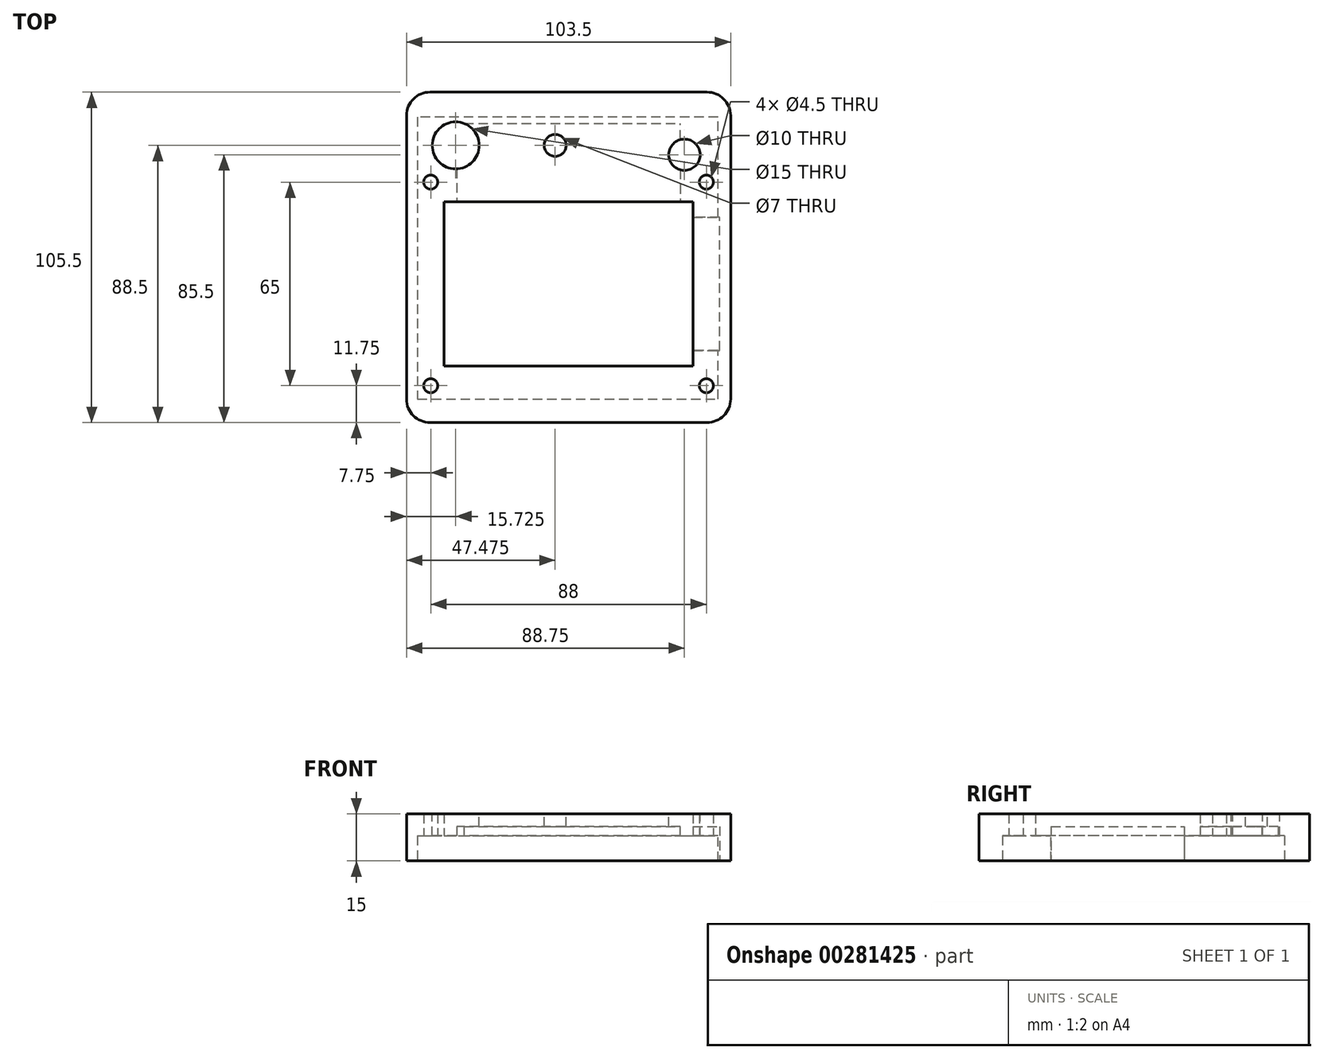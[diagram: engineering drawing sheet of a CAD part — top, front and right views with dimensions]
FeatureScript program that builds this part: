
annotation { "Feature Type Name" : "Feature", "Feature Type Description" : "" }
export const myFeature = defineFeature(function(context is Context, id is Id, definition is map)
    precondition{}
    {
        {
            var Q0;
            Q0=qCreatedBy(makeId("Top.planeOp"),FACE);
            var sketch = newSketch(context, id + "F0", { "sketchPlane" : qUnion([Q0])});
            skLineSegment(sketch, "E0.rect.bottom", {"start": v(44, -32.5) * mm, "end": v(-44, -32.5) * mm, "construction": true});
            skLineSegment(sketch, "E0.rect.top", {"start": v(44, 32.5) * mm, "end": v(-44, 32.5) * mm, "construction": true});
            skLineSegment(sketch, "E0.rect.left", {"start": v(44, -32.5) * mm, "end": v(44, 32.5) * mm, "construction": true});
            skLineSegment(sketch, "E0.rect.right", {"start": v(-44, -32.5) * mm, "end": v(-44, 32.5) * mm, "construction": true});
            skPoint(sketch, "E0.rect.middle", {"position": v(0, 0) * mm});
            skCircle(sketch, "E1", {"center": v(-44, 32.5) * mm, "radius": 2.25 * mm});
            skCircle(sketch, "E2", {"center": v(44, 32.5) * mm, "radius": 2.25 * mm});
            skCircle(sketch, "E3", {"center": v(-44, -32.5) * mm, "radius": 2.25 * mm});
            skCircle(sketch, "E4", {"center": v(44, -32.5) * mm, "radius": 2.25 * mm});
            skLineSegment(sketch, "E5.rect.bottom", {"start": v(39.75, -26.25) * mm, "end": v(-39.75, -26.25) * mm});
            skLineSegment(sketch, "E5.rect.top", {"start": v(39.75, 26.25) * mm, "end": v(-39.75, 26.25) * mm});
            skLineSegment(sketch, "E5.rect.left", {"start": v(39.75, -26.25) * mm, "end": v(39.75, 26.25) * mm});
            skLineSegment(sketch, "E5.rect.right", {"start": v(-39.75, -26.25) * mm, "end": v(-39.75, 26.25) * mm});
            skLineSegment(sketch, "E6", {"start": v(-51.75, -44.25) * mm, "end": v(51.75, -44.25) * mm});
            skLineSegment(sketch, "E7", {"start": v(51.75, -44.25) * mm, "end": v(51.75, 61.25) * mm});
            skLineSegment(sketch, "E8", {"start": v(-3.25, 61.25) * mm, "end": v(-51.75, 61.25) * mm});
            skLineSegment(sketch, "E9", {"start": v(-51.75, 61.25) * mm, "end": v(-51.75, -9.25) * mm});
            skLineSegment(sketch, "E10", {"start": v(-51.75, -9.25) * mm, "end": v(-71.75, -9.25) * mm, "construction": true});
            skLineSegment(sketch, "E11", {"start": v(-71.75, -9.25) * mm, "end": v(-71.75, -44.25) * mm, "construction": true});
            skLineSegment(sketch, "E12", {"start": v(-71.75, -44.25) * mm, "end": v(-51.75, -44.25) * mm, "construction": true});
            skLineSegment(sketch, "E13", {"start": v(11.75, 61.25) * mm, "end": v(11.75, 91.25) * mm, "construction": true});
            skLineSegment(sketch, "E14", {"start": v(11.75, 91.25) * mm, "end": v(51.75, 91.25) * mm, "construction": true});
            skLineSegment(sketch, "E15", {"start": v(51.75, 91.25) * mm, "end": v(51.75, 61.25) * mm, "construction": true});
            skCircle(sketch, "E16", {"center": v(44.25, 83.75) * mm, "radius": 2.12 * mm, "construction": true});
            skCircle(sketch, "E17", {"center": v(-64.25, -16.75) * mm, "radius": 2.12 * mm, "construction": true});
            skCircle(sketch, "E18", {"center": v(-64.25, -36.75) * mm, "radius": 2.12 * mm, "construction": true});
            skCircle(sketch, "E19", {"center": v(4.25, 83.75) * mm, "radius": 2.12 * mm, "construction": true});
            skLineSegment(sketch, "E20", {"start": v(11.75, 61.25) * mm, "end": v(51.75, 61.25) * mm});
            skLineSegment(sketch, "E21", {"start": v(11.75, 91.25) * mm, "end": v(-3.25, 91.25) * mm, "construction": true});
            skLineSegment(sketch, "E22", {"start": v(-3.25, 91.25) * mm, "end": v(-3.25, 61.25) * mm, "construction": true});
            skLineSegment(sketch, "E23", {"start": v(-3.25, 61.25) * mm, "end": v(11.75, 61.25) * mm});
            skLineSegment(sketch, "E24", {"start": v(-51.75, -9.25) * mm, "end": v(-51.75, -44.25) * mm});
            skSolve(sketch);
        }
        {
            var Q0;
            Q0=qSketchRegion(id+"F0",true);
            extrude(context, id + "F1", {"entities" : qUnion([Q0]), "depth" : 15 * mm});
        }
        {
            var Q0;
            Q0=makeQuery(id+"F1.opExtrude","CAP_FACE",FACE,{"disambiguationData":[OSD([sQuery(id+"F0.wireOp",EDGE,"E1"),sQuery(id+"F0.wireOp",EDGE,"E2"),sQuery(id+"F0.wireOp",EDGE,"E3"),sQuery(id+"F0.wireOp",EDGE,"E4"),sQuery(id+"F0.wireOp",EDGE,"35a865c8-fce7-4a90-a9e5-dcc01825e7bf.rect.bottom"),sQuery(id+"F0.wireOp",EDGE,"35a865c8-fce7-4a90-a9e5-dcc01825e7bf.rect.top"),sQuery(id+"F0.wireOp",EDGE,"35a865c8-fce7-4a90-a9e5-dcc01825e7bf.rect.left"),sQuery(id+"F0.wireOp",EDGE,"35a865c8-fce7-4a90-a9e5-dcc01825e7bf.rect.right"),sQuery(id+"F0.wireOp",EDGE,"E5.rect.bottom"),sQuery(id+"F0.wireOp",EDGE,"E5.rect.top"),sQuery(id+"F0.wireOp",EDGE,"E5.rect.left"),sQuery(id+"F0.wireOp",EDGE,"E5.rect.right")])],"isStart":true});
            var sketch = newSketch(context, id + "F2", { "sketchPlane" : qUnion([Q0])});
            skLineSegment(sketch, "E25", {"start": v(39.75, 21.25) * mm, "end": v(48.25, 21.25) * mm});
            skLineSegment(sketch, "E26", {"start": v(48.25, 21.25) * mm, "end": v(48.25, -21.25) * mm});
            skLineSegment(sketch, "E27", {"start": v(48.25, -21.25) * mm, "end": v(39.75, -21.25) * mm});
            skLineSegment(sketch, "E28", {"start": v(39.75, -21.25) * mm, "end": v(39.75, 21.25) * mm});
            skLineSegment(sketch, "E29", {"start": v(-35.75, -26.25) * mm, "end": v(-35.75, -51.25) * mm});
            skLineSegment(sketch, "E30", {"start": v(-35.75, -51.25) * mm, "end": v(35.75, -51.25) * mm});
            skLineSegment(sketch, "E31", {"start": v(35.75, -51.25) * mm, "end": v(35.75, -26.25) * mm});
            skLineSegment(sketch, "E32", {"start": v(35.75, -26.25) * mm, "end": v(-35.75, -26.25) * mm});
            skSolve(sketch);
        }
        {
            var Q0;
            Q0=qSketchRegion(id+"F2",true);
            extrude(context, id + "F3", {"entities" : qUnion([Q0]), "operationType" : NewBodyOperationType.REMOVE, "oppositeDirection" : true, "depth" : 11 * mm});
        }
        {
            var Q0;
            Q0=makeQuery(id+"F1.opExtrude","CAP_FACE",FACE,{"disambiguationData":[OSD([sQuery(id+"F0.wireOp",EDGE,"E1"),sQuery(id+"F0.wireOp",EDGE,"E2"),sQuery(id+"F0.wireOp",EDGE,"E3"),sQuery(id+"F0.wireOp",EDGE,"E4"),sQuery(id+"F0.wireOp",EDGE,"35a865c8-fce7-4a90-a9e5-dcc01825e7bf.rect.bottom"),sQuery(id+"F0.wireOp",EDGE,"35a865c8-fce7-4a90-a9e5-dcc01825e7bf.rect.top"),sQuery(id+"F0.wireOp",EDGE,"35a865c8-fce7-4a90-a9e5-dcc01825e7bf.rect.left"),sQuery(id+"F0.wireOp",EDGE,"35a865c8-fce7-4a90-a9e5-dcc01825e7bf.rect.right"),sQuery(id+"F0.wireOp",EDGE,"E5.rect.bottom"),sQuery(id+"F0.wireOp",EDGE,"E5.rect.top"),sQuery(id+"F0.wireOp",EDGE,"E5.rect.left"),sQuery(id+"F0.wireOp",EDGE,"E5.rect.right")])],"isStart":true});
            var sketch = newSketch(context, id + "F4", { "sketchPlane" : qUnion([Q0])});
            skLineSegment(sketch, "E33", {"start": v(-48.25, 36.75) * mm, "end": v(47.75, 36.75) * mm});
            skLineSegment(sketch, "E34", {"start": v(47.75, 36.75) * mm, "end": v(47.75, -53.25) * mm});
            skLineSegment(sketch, "E35", {"start": v(47.75, -53.25) * mm, "end": v(-48.25, -53.25) * mm});
            skLineSegment(sketch, "E36", {"start": v(-48.25, -53.25) * mm, "end": v(-48.25, 36.75) * mm});
            skSolve(sketch);
        }
        {
            var Q0;
            Q0=qSketchRegion(id+"F4",true);
            extrude(context, id + "F5", {"entities" : qUnion([Q0]), "operationType" : NewBodyOperationType.REMOVE, "oppositeDirection" : true, "depth" : 8 * mm});
        }
        {
            var Q0;
            Q0=makeQuery(id+"F1.opExtrude","CAP_FACE",FACE,{"disambiguationData":[OSD([sQuery(id+"F0.wireOp",EDGE,"E1"),sQuery(id+"F0.wireOp",EDGE,"E2"),sQuery(id+"F0.wireOp",EDGE,"E3"),sQuery(id+"F0.wireOp",EDGE,"E4"),sQuery(id+"F0.wireOp",EDGE,"35a865c8-fce7-4a90-a9e5-dcc01825e7bf.rect.bottom"),sQuery(id+"F0.wireOp",EDGE,"35a865c8-fce7-4a90-a9e5-dcc01825e7bf.rect.top"),sQuery(id+"F0.wireOp",EDGE,"35a865c8-fce7-4a90-a9e5-dcc01825e7bf.rect.left"),sQuery(id+"F0.wireOp",EDGE,"35a865c8-fce7-4a90-a9e5-dcc01825e7bf.rect.right"),sQuery(id+"F0.wireOp",EDGE,"E5.rect.bottom"),sQuery(id+"F0.wireOp",EDGE,"E5.rect.top"),sQuery(id+"F0.wireOp",EDGE,"E5.rect.left"),sQuery(id+"F0.wireOp",EDGE,"E5.rect.right")])],"isStart":false});
            var sketch = newSketch(context, id + "F6", { "sketchPlane" : qUnion([Q0])});
            skCircle(sketch, "E37", {"center": v(-36.02, 44.25) * mm, "radius": 7.5 * mm});
            skCircle(sketch, "E38", {"center": v(-4.27, 44.25) * mm, "radius": 3.5 * mm});
            skCircle(sketch, "E39", {"center": v(37, 41.25) * mm, "radius": 5 * mm});
            skSolve(sketch);
        }
        {
            var Q0;
            Q0=qSketchRegion(id+"F6",true);
            extrude(context, id + "F7", {"entities" : qUnion([Q0]), "operationType" : NewBodyOperationType.REMOVE, "endBound" : BoundingType.THROUGH_ALL, "oppositeDirection" : true, "depth" : 25 * mm});
        }
        {
            var Q0;
            Q0=makeQuery(id+"F1.opExtrude","SWEPT_EDGE",EDGE,{"disambiguationData":[OSD([sQuery(id+"F0.wireOp",EDGE,"E6"),sQuery(id+"F0.wireOp",EDGE,"E7")])]});
            var Q1;
            Q1=makeQuery(id+"F1.opExtrude","SWEPT_EDGE",EDGE,{"disambiguationData":[OSD([sQuery(id+"F0.wireOp",EDGE,"E6"),sQuery(id+"F0.wireOp",EDGE,"E9")])]});
            var Q2;
            Q2=makeQuery(id+"F1.opExtrude","SWEPT_EDGE",EDGE,{"disambiguationData":[OSD([sQuery(id+"F0.wireOp",EDGE,"E7"),sQuery(id+"F0.wireOp",EDGE,"E8")])]});
            var Q3;
            Q3=makeQuery(id+"F1.opExtrude","SWEPT_EDGE",EDGE,{"disambiguationData":[OSD([sQuery(id+"F0.wireOp",EDGE,"E8"),sQuery(id+"F0.wireOp",EDGE,"E9")])]});
            var Q4;
            Q4=makeQuery(id+"F1.opExtrude","SWEPT_EDGE",EDGE,{"disambiguationData":[OSD([sQuery(id+"F0.wireOp",EDGE,"E14"),sQuery(id+"F0.wireOp",EDGE,"E15")])]});
            var Q5;
            Q5=makeQuery(id+"F1.opExtrude","SWEPT_EDGE",EDGE,{"disambiguationData":[OSD([sQuery(id+"F0.wireOp",EDGE,"E13"),sQuery(id+"F0.wireOp",EDGE,"E14")])]});
            var Q6;
            Q6=makeQuery(id+"F1.opExtrude","SWEPT_EDGE",EDGE,{"disambiguationData":[OSD([sQuery(id+"F0.wireOp",EDGE,"E10"),sQuery(id+"F0.wireOp",EDGE,"E11")])]});
            var Q7;
            Q7=makeQuery(id+"F1.opExtrude","SWEPT_EDGE",EDGE,{"disambiguationData":[OSD([sQuery(id+"F0.wireOp",EDGE,"E11"),sQuery(id+"F0.wireOp",EDGE,"E12")])]});
            fillet(context, id + "F8", {"entities" : qUnion([Q0, Q1, Q2, Q3, Q4, Q5, Q6, Q7]), "radius" : 7.5 * mm, "tangentPropagation" : true, "allowEdgeOverflow" : false});
        }
    });
